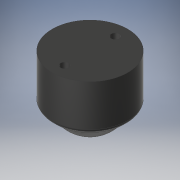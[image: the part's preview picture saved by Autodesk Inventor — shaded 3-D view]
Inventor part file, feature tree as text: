
AUTODESK INVENTOR PART (.ipt)
format: ipt  version: 2019.4 (Build 234330000, 330)  size: 187,392 bytes
history: native  units: mm
features: plane x3, sketch x3, extrude x2, revolve x1, chamfer x1, fillet x1
ambient origin geometry x8: Origin, YZ Plane, XZ Plane, XY Plane, X Axis, Y Axis, Z Axis, Center Point
bodies: Solid4 (feature_tree)
feature tree (11):
  revolve  "Revolution1"  Angle=90.0deg
  plane  "Work Plane1"
  plane  "Work Plane3"
  extrude  "Extrusion1"  Depth=14.6mm
  chamfer  "Chamfer1"  Distance=14.6mm
  fillet  "Fillet1"  Radius=1.0mm
  extrude  "Extrusion2"  Depth=14.6mm
  sketch  "Sketch1"  dims[d0=19.05mm d1=90.0deg]
  sketch  "Sketch2"  dims[d2=23.0mm d3=-19.05mm d4=20.7mm d5=14.6mm d6=0.0mm]
  plane  "Work Plane2"
  sketch  "Sketch3"  dims[d7=1.5mm d8=2.0mm d9=45.0deg d10=1.0mm d11=15.4mm d12=2.54mm d13=2.54mm d14=14.6mm d15=0.0mm]
